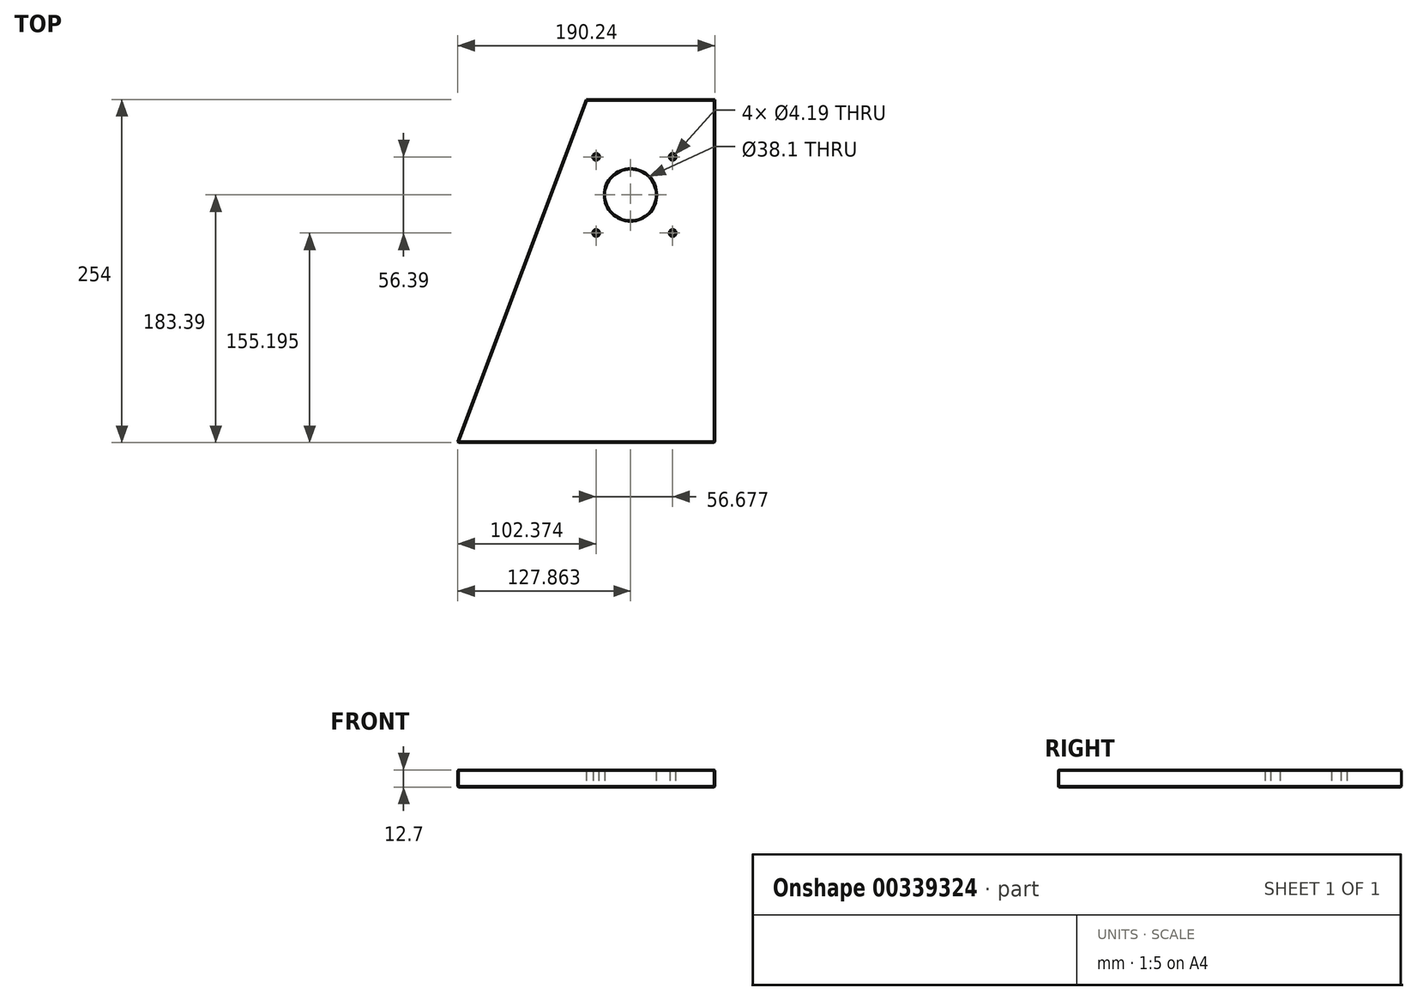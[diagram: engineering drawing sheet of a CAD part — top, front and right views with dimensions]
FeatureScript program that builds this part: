
annotation { "Feature Type Name" : "Feature", "Feature Type Description" : "" }
export const myFeature = defineFeature(function(context is Context, id is Id, definition is map)
    precondition{}
    {
        {
            var Q0;
            Q0=qCreatedBy(makeId("Top.planeOp"),FACE);
            var sketch = newSketch(context, id + "F0", { "sketchPlane" : qUnion([Q0])});
            skLineSegment(sketch, "E0.top", {"start": v(95.25, -127) * mm, "end": v(-95.25, -127) * mm});
            skLineSegment(sketch, "E0.left", {"start": v(95.25, 127) * mm, "end": v(95.25, -127) * mm});
            skPoint(sketch, "E0.middle", {"position": v(0, 0) * mm});
            skLineSegment(sketch, "E1", {"start": v(-95.25, -127) * mm, "end": v(0, 127) * mm});
            skLineSegment(sketch, "E2", {"start": v(0, 127) * mm, "end": v(95.25, 127) * mm});
            skCircle(sketch, "E3", {"center": v(32.87, 56.39) * mm, "radius": 19.05 * mm});
            skCircle(sketch, "E4", {"center": v(7.38, 28.2) * mm, "radius": 2.1 * mm});
            skCircle(sketch, "E5", {"center": v(64.06, 28.2) * mm, "radius": 2.1 * mm});
            skCircle(sketch, "E6.MirrorC", {"center": v(64.06, 84.58) * mm, "radius": 2.1 * mm});
            skCircle(sketch, "E7.MirrorC", {"center": v(7.38, 84.58) * mm, "radius": 2.1 * mm});
            skSolve(sketch);
        }
        {
            var Q0;
            Q0 = qSketchRegion(id + "F0", true);
            extrude(context, id + "F1", {"entities" : qUnion([Q0]), "depth" : 12.7 * mm});
        }
        {
            var Q0;
            Q0=makeQuery(id+"F1.opExtrude","CAP_EDGE",EDGE,{"disambiguationData":[OSD([sQuery(id+"F0.wireOp",EDGE,"E7.MirrorC")])],"isStart":false});
            var Q1;
            Q1=makeQuery(id+"F1.opExtrude","CAP_EDGE",EDGE,{"disambiguationData":[OSD([sQuery(id+"F0.wireOp",EDGE,"E6.MirrorC")])],"isStart":false});
            var Q2;
            Q2=makeQuery(id+"F1.opExtrude","CAP_EDGE",EDGE,{"disambiguationData":[OSD([sQuery(id+"F0.wireOp",EDGE,"E3")])],"isStart":false});
            var Q3;
            Q3=makeQuery(id+"F1.opExtrude","CAP_EDGE",EDGE,{"disambiguationData":[OSD([sQuery(id+"F0.wireOp",EDGE,"E4")])],"isStart":false});
            var Q4;
            Q4=makeQuery(id+"F1.opExtrude","CAP_EDGE",EDGE,{"disambiguationData":[OSD([sQuery(id+"F0.wireOp",EDGE,"E5")])],"isStart":false});
            var Q5;
            Q5=makeQuery(id+"F1.opExtrude","CAP_EDGE",EDGE,{"disambiguationData":[OSD([sQuery(id+"F0.wireOp",EDGE,"E6.MirrorC")])],"isStart":true});
            var Q6;
            Q6=makeQuery(id+"F1.opExtrude","CAP_EDGE",EDGE,{"disambiguationData":[OSD([sQuery(id+"F0.wireOp",EDGE,"E7.MirrorC")])],"isStart":true});
            var Q7;
            Q7=makeQuery(id+"F1.opExtrude","CAP_EDGE",EDGE,{"disambiguationData":[OSD([sQuery(id+"F0.wireOp",EDGE,"E3")])],"isStart":true});
            var Q8;
            Q8=makeQuery(id+"F1.opExtrude","CAP_EDGE",EDGE,{"disambiguationData":[OSD([sQuery(id+"F0.wireOp",EDGE,"E5")])],"isStart":true});
            var Q9;
            Q9=makeQuery(id+"F1.opExtrude","CAP_EDGE",EDGE,{"disambiguationData":[OSD([sQuery(id+"F0.wireOp",EDGE,"E4")])],"isStart":true});
            var Q10;
            Q10=makeQuery(id+"F1.opExtrude","CAP_EDGE",EDGE,{"disambiguationData":[OSD([sQuery(id+"F0.wireOp",EDGE,"E1")])],"isStart":true});
            var Q11;
            Q11=makeQuery(id+"F1.opExtrude","CAP_EDGE",EDGE,{"disambiguationData":[OSD([sQuery(id+"F0.wireOp",EDGE,"E0.left")])],"isStart":true});
            var Q12;
            Q12=makeQuery(id+"F1.opExtrude","CAP_EDGE",EDGE,{"disambiguationData":[OSD([sQuery(id+"F0.wireOp",EDGE,"E2")])],"isStart":true});
            var Q13;
            Q13=makeQuery(id+"F1.opExtrude","CAP_EDGE",EDGE,{"disambiguationData":[OSD([sQuery(id+"F0.wireOp",EDGE,"E0.top")])],"isStart":true});
            var Q14;
            Q14=makeQuery(id+"F1.opExtrude","SWEPT_EDGE",EDGE,{"disambiguationData":[OSD([sQuery(id+"F0.wireOp",EDGE,"E0.top"),sQuery(id+"F0.wireOp",EDGE,"E1")])]});
            var Q15;
            Q15=makeQuery(id+"F1.opExtrude","SWEPT_EDGE",EDGE,{"disambiguationData":[OSD([sQuery(id+"F0.wireOp",EDGE,"E0.top"),sQuery(id+"F0.wireOp",EDGE,"E0.left")])]});
            var Q16;
            Q16=makeQuery(id+"F1.opExtrude","CAP_EDGE",EDGE,{"disambiguationData":[OSD([sQuery(id+"F0.wireOp",EDGE,"E0.top")])],"isStart":false});
            var Q17;
            Q17=makeQuery(id+"F1.opExtrude","CAP_EDGE",EDGE,{"disambiguationData":[OSD([sQuery(id+"F0.wireOp",EDGE,"E1")])],"isStart":false});
            var Q18;
            Q18=makeQuery(id+"F1.opExtrude","CAP_EDGE",EDGE,{"disambiguationData":[OSD([sQuery(id+"F0.wireOp",EDGE,"E0.left")])],"isStart":false});
            var Q19;
            Q19=makeQuery(id+"F1.opExtrude","CAP_EDGE",EDGE,{"disambiguationData":[OSD([sQuery(id+"F0.wireOp",EDGE,"E2")])],"isStart":false});
            chamfer(context, id + "F2", {"entities" : qUnion([Q0, Q1, Q2, Q3, Q4, Q5, Q6, Q7, Q8, Q9, Q10, Q11, Q12, Q13, Q14, Q15, Q16, Q17, Q18, Q19]), "width" : 0.5 * mm, "tangentPropagation" : true});
        }
    });
